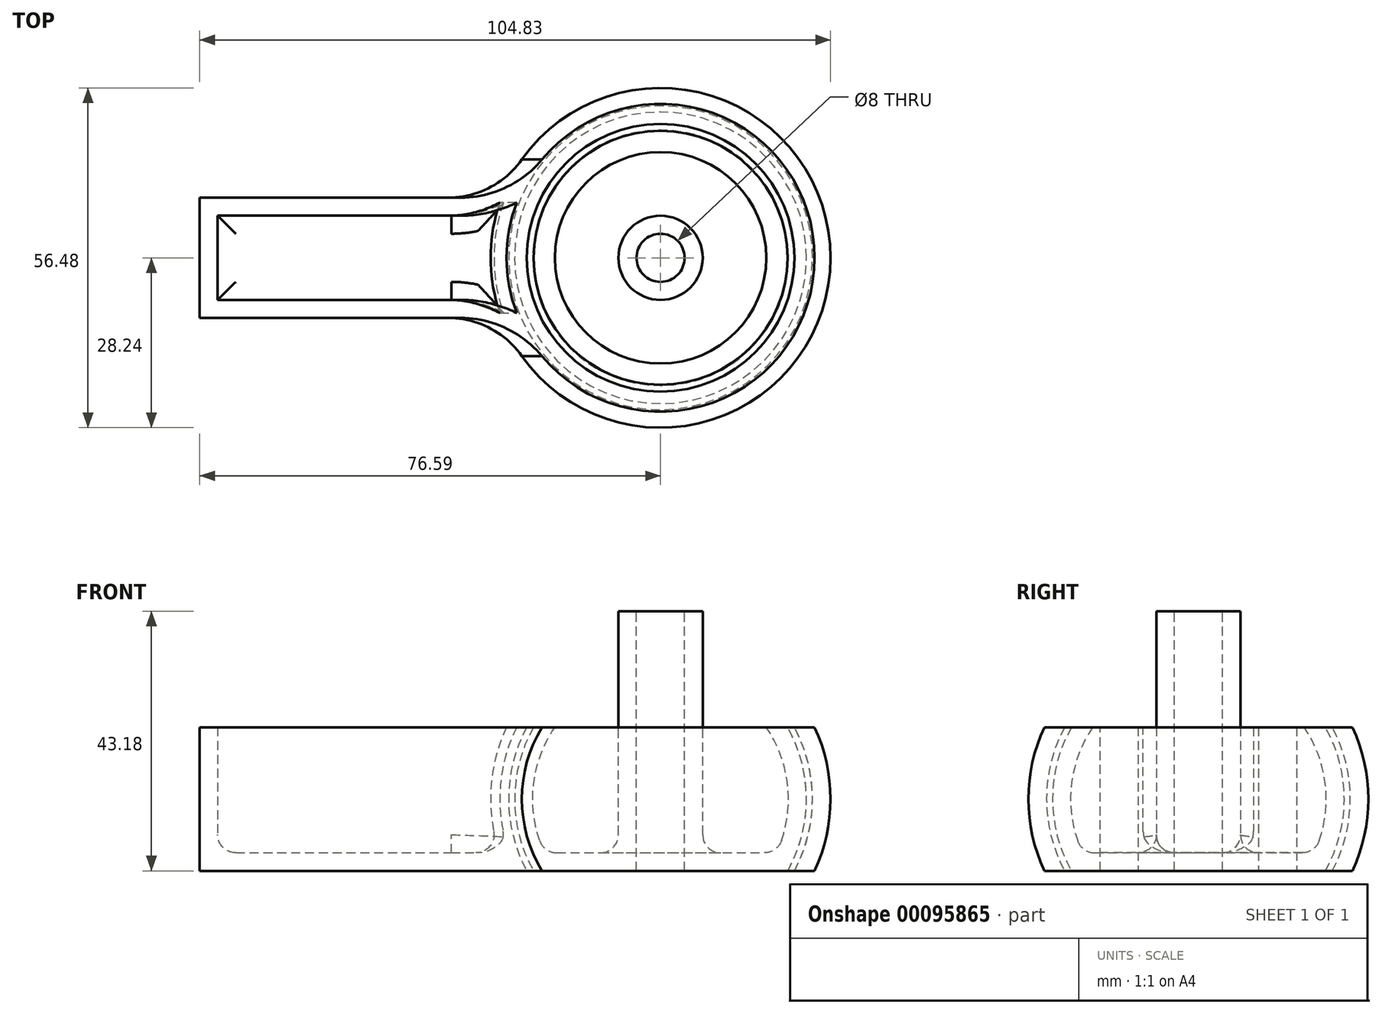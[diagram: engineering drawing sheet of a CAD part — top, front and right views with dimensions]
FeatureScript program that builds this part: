
annotation { "Feature Type Name" : "Feature", "Feature Type Description" : "" }
export const myFeature = defineFeature(function(context is Context, id is Id, definition is map)
    precondition{}
    {
        {
            var Q0;
            Q0=qCreatedBy(makeId("Front.planeOp"),FACE);
            var sketch = newSketch(context, id + "F0", { "sketchPlane" : qUnion([Q0])});
            skCircle(sketch, "E0", {"center": v(0, 0) * mm, "radius": 24.24 * mm});
            skCircle(sketch, "E1", {"center": v(0, 0) * mm, "radius": 25.24 * mm});
            skCircle(sketch, "E2", {"center": v(0, 0) * mm, "radius": 28.24 * mm});
            skLineSegment(sketch, "E3", {"start": v(-7, 23.21) * mm, "end": v(-7, 31.24) * mm});
            skLineSegment(sketch, "E4", {"start": v(-7, 31.24) * mm, "end": v(0, 31.24) * mm});
            skLineSegment(sketch, "E5", {"start": v(0, 31.24) * mm, "end": v(0, 24.24) * mm});
            skLineSegment(sketch, "E6.MirrorCS", {"start": v(7, 31.24) * mm, "end": v(0, 31.24) * mm});
            skLineSegment(sketch, "E7.MirrorCS", {"start": v(7, 23.21) * mm, "end": v(7, 31.24) * mm});
            skLineSegment(sketch, "E8", {"start": v(-4, 31.24) * mm, "end": v(-4, -23.91) * mm});
            skLineSegment(sketch, "E9", {"start": v(0, 24.24) * mm, "end": v(0, -28.24) * mm});
            skPoint(sketch, "E10", {"position": v(-24.24, 0) * mm});
            skLineSegment(sketch, "E11", {"start": v(-25.6, 11.94) * mm, "end": v(-22.24, 11.94) * mm, "construction": true});
            skLineSegment(sketch, "E12", {"start": v(0, 0) * mm, "end": v(-24.89, 13.35) * mm, "construction": true});
            skLineSegment(sketch, "E13", {"start": v(-25.6, 11.94) * mm, "end": v(0, 11.94) * mm});
            skLineSegment(sketch, "E14.MirrorCS", {"start": v(-25.6, -11.94) * mm, "end": v(0, -11.94) * mm});
            skLineSegment(sketch, "E15", {"start": v(0, 0) * mm, "end": v(-7, 23.21) * mm, "construction": true});
            skLineSegment(sketch, "E16", {"start": v(-25.6, 11.94) * mm, "end": v(-76.6, 11.94) * mm});
            skLineSegment(sketch, "E17", {"start": v(-76.6, 11.94) * mm, "end": v(-76.6, -11.94) * mm});
            skLineSegment(sketch, "E18", {"start": v(-76.6, -11.94) * mm, "end": v(-25.6, -11.94) * mm});
            skLineSegment(sketch, "E19", {"start": v(-7, 23.21) * mm, "end": v(-7, 11.94) * mm});
            skSolve(sketch);
        }
        {
            var Q0;
            {var subQ0=sQuery(id+"F0.wireOp",EDGE,"E13");var subQ1=sQuery(id+"F0.wireOp",EDGE,"E1");var subQ2=makeQuery(id+"F0.imprint","INTERSECT",VERTEX,{"derivedFrom":[subQ1,subQ0]});Q0=makeQuery(id+"F0.imprint","IMPRINT",FACE,{"disambiguationData":[TD([[makeQuery(id+"F0.imprint","IMPRINT",EDGE,{"disambiguationData":[TD([[subQ2,-1.0]])],"derivedFrom":subQ1}),-1.0]])]});}
            var Q1;
            {var subQ0=sQuery(id+"F0.wireOp",EDGE,"E13");var subQ1=sQuery(id+"F0.wireOp",EDGE,"E0");var subQ2=makeQuery(id+"F0.imprint","INTERSECT",VERTEX,{"derivedFrom":[subQ1,subQ0]});Q1=makeQuery(id+"F0.imprint","IMPRINT",FACE,{"disambiguationData":[TD([[makeQuery(id+"F0.imprint","IMPRINT",EDGE,{"disambiguationData":[TD([[subQ2,-1.0]])],"derivedFrom":subQ1}),1.0]])]});}
            var Q2;
            {var subQ0=sQuery(id+"F0.wireOp",EDGE,"E0");var subQ1=makeQuery(id+"F0.imprint","INTERSECT",VERTEX,{"derivedFrom":[subQ0,sQuery(id+"F0.wireOp",EDGE,"E3")]});Q2=makeQuery(id+"F0.imprint","IMPRINT",FACE,{"disambiguationData":[TD([[makeQuery(id+"F0.imprint","IMPRINT",EDGE,{"disambiguationData":[TD([[subQ1,1.0]])],"derivedFrom":subQ0}),1.0]])]});}
            var Q3;
            {var subQ0=sQuery(id+"F0.wireOp",EDGE,"E3");var subQ1=sQuery(id+"F0.wireOp",EDGE,"E0");var subQ2=makeQuery(id+"F0.imprint","INTERSECT",VERTEX,{"derivedFrom":[subQ1,subQ0]});Q3=makeQuery(id+"F0.imprint","IMPRINT",FACE,{"disambiguationData":[TD([[makeQuery(id+"F0.imprint","IMPRINT",EDGE,{"disambiguationData":[TD([[subQ2,1.0]])],"derivedFrom":subQ1}),-1.0]])]});}
            var Q4;
            {var subQ0=sQuery(id+"F0.wireOp",EDGE,"E8");var subQ1=sQuery(id+"F0.wireOp",EDGE,"E1");var subQ2=makeQuery(id+"F0.imprint","INTERSECT",VERTEX,{"derivedFrom":[subQ1,subQ0]});Q4=makeQuery(id+"F0.imprint","IMPRINT",FACE,{"disambiguationData":[TD([[makeQuery(id+"F0.imprint","IMPRINT",EDGE,{"disambiguationData":[TD([[subQ2,-1.0]])],"derivedFrom":subQ1}),-1.0]])]});}
            var Q5;
            {var subQ0=sQuery(id+"F0.wireOp",EDGE,"E3");var subQ1=sQuery(id+"F0.wireOp",EDGE,"E2");var subQ2=makeQuery(id+"F0.imprint","INTERSECT",VERTEX,{"derivedFrom":[subQ1,subQ0]});Q5=makeQuery(id+"F0.imprint","IMPRINT",FACE,{"disambiguationData":[TD([[makeQuery(id+"F0.imprint","IMPRINT",EDGE,{"disambiguationData":[TD([[subQ2,1.0]])],"derivedFrom":subQ1}),-1.0]])]});}
            var Q6;
            Q6=sQuery(id+"F0.wireOp",EDGE,"E5");
            revolve(context, id + "F1", {"entities" : qUnion([Q0, Q1, Q2, Q3, Q4, Q5]), "axis" : qUnion([Q6]), "revolveType" : RevolveType.FULL});
        }
        {
            var Q0;
            {var subQ0=sQuery(id+"F0.wireOp",EDGE,"E13");var subQ1=sQuery(id+"F0.wireOp",EDGE,"E1");var subQ2=makeQuery(id+"F0.imprint","INTERSECT",VERTEX,{"derivedFrom":[subQ1,subQ0]});Q0=makeQuery(id+"F0.imprint","IMPRINT",FACE,{"disambiguationData":[TD([[makeQuery(id+"F0.imprint","IMPRINT",EDGE,{"disambiguationData":[TD([[subQ2,-1.0]])],"derivedFrom":subQ1}),-1.0]])]});}
            var Q1;
            {var subQ0=sQuery(id+"F0.wireOp",EDGE,"E16");Q1=makeQuery(id+"F0.imprint","IMPRINT",FACE,{"disambiguationData":[TD([[makeQuery(id+"F0.imprint","IMPRINT",EDGE,{"derivedFrom":subQ0}),1.0]])]});}
            extrude(context, id + "F2", {"entities" : qUnion([Q0, Q1]), "operationType" : NewBodyOperationType.ADD, "endBound" : BoundingType.SYMMETRIC, "depth" : 20 * mm});
        }
        {
            var Q0;
            Q0=makeQuery(id+"F2.boolean.opBoolean","INTERSECT",EDGE,{"derivedFrom":[makeQuery(id+"F1.opRevolve","SWEPT_FACE",FACE,{"disambiguationData":[OSD([sQuery(id+"F0.wireOp",EDGE,"E2")])]}),makeQuery(id+"F2.opExtrude","CAP_FACE",FACE,{"disambiguationData":[OSD([sQuery(id+"F0.wireOp",EDGE,"E1"),sQuery(id+"F0.wireOp",EDGE,"E13"),sQuery(id+"F0.wireOp",EDGE,"E14.MirrorCS"),sQuery(id+"F0.wireOp",EDGE,"E16"),sQuery(id+"F0.wireOp",EDGE,"E17"),sQuery(id+"F0.wireOp",EDGE,"E18")])],"isStart":false})]});
            var Q1;
            Q1=makeQuery(id+"F2.boolean.opBoolean","INTERSECT",EDGE,{"derivedFrom":[makeQuery(id+"F1.opRevolve","SWEPT_FACE",FACE,{"disambiguationData":[OSD([sQuery(id+"F0.wireOp",EDGE,"E2")])]}),makeQuery(id+"F2.opExtrude","CAP_FACE",FACE,{"disambiguationData":[OSD([sQuery(id+"F0.wireOp",EDGE,"E1"),sQuery(id+"F0.wireOp",EDGE,"E13"),sQuery(id+"F0.wireOp",EDGE,"E14.MirrorCS"),sQuery(id+"F0.wireOp",EDGE,"E16"),sQuery(id+"F0.wireOp",EDGE,"E17"),sQuery(id+"F0.wireOp",EDGE,"E18")])],"isStart":true})]});
            fillet(context, id + "F3", {"entities" : qUnion([Q0, Q1]), "radius" : 15 * mm, "tangentPropagation" : true, "allowEdgeOverflow" : false});
        }
        {
            var Q0;
            {var subQ0=sQuery(id+"F0.wireOp",EDGE,"E13");Q0=makeQuery(id+"F1.opRevolve","SWEPT_FACE",FACE,{"disambiguationData":[OSD([subQ0]),TDD([makeQuery(id+"F0.imprint","IMPRINT",EDGE,{"disambiguationData":[TD([[makeQuery(id+"F0.imprint","INTERSECT",VERTEX,{"derivedFrom":[subQ0,sQuery(id+"F0.wireOp",EDGE,"E19")]}),1.0]])],"derivedFrom":subQ0})])]});}
            var Q1;
            {var subQ0=sQuery(id+"F0.wireOp",EDGE,"E16");var subQ1=sQuery(id+"F0.wireOp",EDGE,"E13");Q1=makeQuery(id+"F2.boolean.opBoolean","MERGE",FACE,{"derivedFrom":[makeQuery(id+"F1.opRevolve","SWEPT_FACE",FACE,{"disambiguationData":[OSD([subQ1]),TDD([makeQuery(id+"F0.imprint","IMPRINT",EDGE,{"disambiguationData":[TD([[makeQuery(id+"F0.imprint","INTERSECT",VERTEX,{"derivedFrom":[sQuery(id+"F0.wireOp",EDGE,"E1"),subQ1]}),1.0]])],"derivedFrom":subQ1})])]}),makeQuery(id+"F2.opExtrude","SWEPT_FACE",FACE,{"disambiguationData":[OSD([subQ1,subQ0])]})]});}
            shell(context, id + "F4", {"entities" : qUnion([Q0, Q1]), "thickness" : 3 * mm});
        }
        {
            var Q0;
            Q0=makeQuery(id+"F4.opShell","OFFSET_FACE",FACE,{"disambiguationData":[OSD([sQuery(id+"F0.wireOp",EDGE,"E14.MirrorCS"),sQuery(id+"F0.wireOp",EDGE,"E18")])]});
            var Q1;
            Q1=makeQuery(id+"F4.opShell","OFFSET_FACE",FACE,{"disambiguationData":[OSD([sQuery(id+"F0.wireOp",EDGE,"E14.MirrorCS")])]});
            fillet(context, id + "F5", {"entities" : qUnion([Q0, Q1]), "radius" : 3 * mm, "tangentPropagation" : true, "allowEdgeOverflow" : false});
        }
    });
